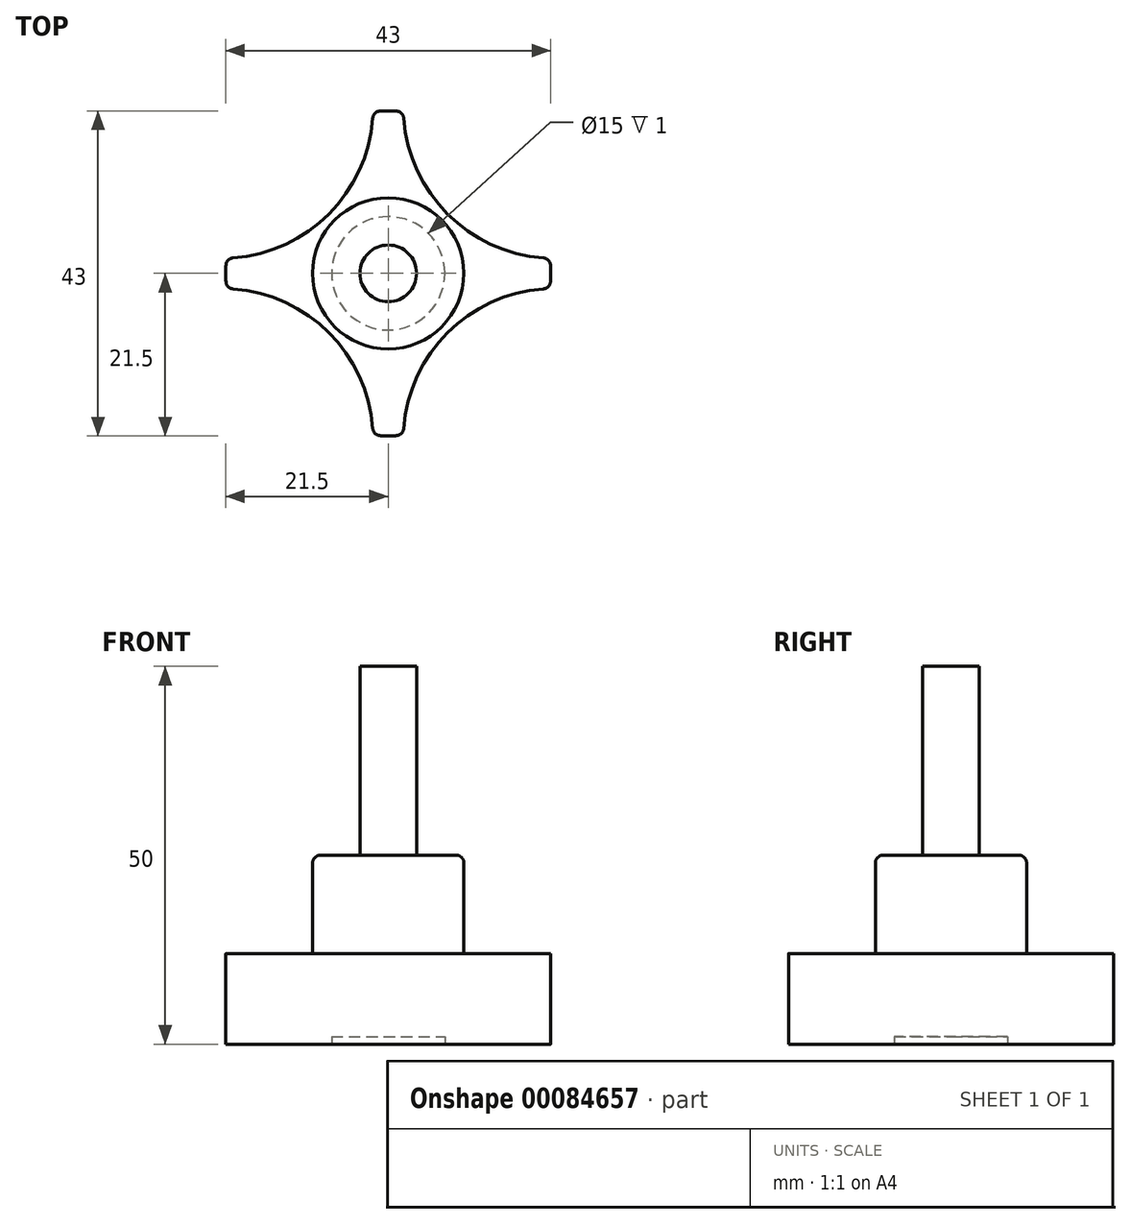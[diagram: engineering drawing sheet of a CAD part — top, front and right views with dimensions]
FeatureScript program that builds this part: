
annotation { "Feature Type Name" : "Feature", "Feature Type Description" : "" }
export const myFeature = defineFeature(function(context is Context, id is Id, definition is map)
    precondition{}
    {
        {
            var Q0;
            Q0=qCreatedBy(makeId("Top.planeOp"),FACE);
            var sketch = newSketch(context, id + "F0", { "sketchPlane" : qUnion([Q0])});
            skLineSegment(sketch, "E0", {"start": v(0, 50) * mm, "end": v(2, 50) * mm});
            skLineSegment(sketch, "E1", {"start": v(50, 0) * mm, "end": v(50, -2) * mm});
            skLineSegment(sketch, "E2.MirrorCS", {"start": v(50, 0) * mm, "end": v(50, 2) * mm});
            skLineSegment(sketch, "E3.MirrorCS", {"start": v(0, -50) * mm, "end": v(2, -50) * mm});
            skLineSegment(sketch, "E4.MirrorCS", {"start": v(-50, 0) * mm, "end": v(-50, 2) * mm});
            skLineSegment(sketch, "E5.MirrorCS", {"start": v(-50, 0) * mm, "end": v(-50, -2) * mm});
            skLineSegment(sketch, "E6.MirrorCS", {"start": v(0, 50) * mm, "end": v(-2, 50) * mm});
            skLineSegment(sketch, "E7.MirrorCS", {"start": v(0, -50) * mm, "end": v(-2, -50) * mm});
            skCircle(sketch, "E8", {"center": v(0, 0) * mm, "radius": 3.75 * mm});
            skCircle(sketch, "E9", {"center": v(0, 0) * mm, "radius": 10 * mm});
            skArc(sketch, "E10", {"start": v(-21.4, 2) * mm, "mid": v(-21.5, 0) * mm, "end": v(-21.4, -2) * mm});
            skLineSegment(sketch, "E11", {"start": v(0, 0) * mm, "end": v(47.67, 47.67) * mm, "construction": true});
            skPoint(sketch, "E12", {"position": v(-21.4, 2) * mm});
            skPoint(sketch, "E13", {"position": v(-2, 21.4) * mm});
            skPoint(sketch, "E14.MirrorP", {"position": v(-21.4, -2) * mm});
            skPoint(sketch, "E15.MirrorP", {"position": v(-2, -21.4) * mm});
            skPoint(sketch, "E16.MirrorP", {"position": v(2, 21.4) * mm});
            skPoint(sketch, "E17.MirrorP", {"position": v(21.4, 2) * mm});
            skPoint(sketch, "E18.MirrorP", {"position": v(21.4, -2) * mm});
            skPoint(sketch, "E19.MirrorP", {"position": v(2, -21.4) * mm});
            skArc(sketch, "E20", {"start": v(21.4, 2) * mm, "mid": v(7.85, 7.85) * mm, "end": v(2, 21.4) * mm});
            skArc(sketch, "E21.MirrorCS", {"start": v(-21.4, 2) * mm, "mid": v(-7.85, 7.85) * mm, "end": v(-2, 21.4) * mm});
            skArc(sketch, "E22.MirrorCS", {"start": v(-21.4, -2) * mm, "mid": v(-7.85, -7.85) * mm, "end": v(-2, -21.4) * mm});
            skArc(sketch, "E23.MirrorCS", {"start": v(21.4, -2) * mm, "mid": v(7.85, -7.85) * mm, "end": v(2, -21.4) * mm});
            skArc(sketch, "E24.trimOffspring", {"start": v(2, 21.4) * mm, "mid": v(0, 21.5) * mm, "end": v(-2, 21.4) * mm});
            skArc(sketch, "E25.trimOffspring", {"start": v(21.4, -2) * mm, "mid": v(21.5, 0) * mm, "end": v(21.4, 2) * mm});
            skArc(sketch, "E26.trimOffspring", {"start": v(-2, -21.4) * mm, "mid": v(0, -21.5) * mm, "end": v(2, -21.4) * mm});
            skSolve(sketch);
        }
        {
            var Q0;
            Q0 = qSketchRegion(id + "F0", true);
            extrude(context, id + "F1", {"entities" : qUnion([Q0]), "depth" : 12 * mm});
        }
        {
            var Q0;
            Q0=makeQuery(id+"F1.opExtrude","SWEPT_EDGE",EDGE,{"disambiguationData":[OSD([sQuery(id+"F0.wireOp",EDGE,"E21.MirrorCS"),sQuery(id+"F0.wireOp",EDGE,"E24.trimOffspring")])]});
            var Q1;
            Q1=makeQuery(id+"F1.opExtrude","SWEPT_EDGE",EDGE,{"disambiguationData":[OSD([sQuery(id+"F0.wireOp",EDGE,"E20"),sQuery(id+"F0.wireOp",EDGE,"E24.trimOffspring")])]});
            var Q2;
            Q2=makeQuery(id+"F1.opExtrude","SWEPT_EDGE",EDGE,{"disambiguationData":[OSD([sQuery(id+"F0.wireOp",EDGE,"E20"),sQuery(id+"F0.wireOp",EDGE,"E25.trimOffspring")])]});
            var Q3;
            Q3=makeQuery(id+"F1.opExtrude","SWEPT_EDGE",EDGE,{"disambiguationData":[OSD([sQuery(id+"F0.wireOp",EDGE,"E23.MirrorCS"),sQuery(id+"F0.wireOp",EDGE,"E25.trimOffspring")])]});
            var Q4;
            Q4=makeQuery(id+"F1.opExtrude","SWEPT_EDGE",EDGE,{"disambiguationData":[OSD([sQuery(id+"F0.wireOp",EDGE,"E23.MirrorCS"),sQuery(id+"F0.wireOp",EDGE,"E26.trimOffspring")])]});
            var Q5;
            Q5=makeQuery(id+"F1.opExtrude","SWEPT_EDGE",EDGE,{"disambiguationData":[OSD([sQuery(id+"F0.wireOp",EDGE,"E22.MirrorCS"),sQuery(id+"F0.wireOp",EDGE,"E26.trimOffspring")])]});
            var Q6;
            Q6=makeQuery(id+"F1.opExtrude","SWEPT_EDGE",EDGE,{"disambiguationData":[OSD([sQuery(id+"F0.wireOp",EDGE,"E10"),sQuery(id+"F0.wireOp",EDGE,"E22.MirrorCS")])]});
            var Q7;
            Q7=makeQuery(id+"F1.opExtrude","SWEPT_EDGE",EDGE,{"disambiguationData":[OSD([sQuery(id+"F0.wireOp",EDGE,"E10"),sQuery(id+"F0.wireOp",EDGE,"E21.MirrorCS")])]});
            fillet(context, id + "F2", {"entities" : qUnion([Q0, Q1, Q2, Q3, Q4, Q5, Q6, Q7]), "radius" : 1 * mm, "tangentPropagation" : true, "allowEdgeOverflow" : false});
        }
        {
            var Q0;
            Q0=makeQuery(id+"F0.imprint","IMPRINT",FACE,{"disambiguationData":[TD([[makeQuery(id+"F0.imprint","IMPRINT",EDGE,{"derivedFrom":sQuery(id+"F0.wireOp",EDGE,"E8")}),-1.0]])]});
            extrude(context, id + "F3", {"entities" : qUnion([Q0]), "operationType" : NewBodyOperationType.ADD, "depth" : 25 * mm});
        }
        {
            var Q0;
            Q0=makeQuery(id+"F0.imprint","IMPRINT",FACE,{"disambiguationData":[TD([[makeQuery(id+"F0.imprint","IMPRINT",EDGE,{"derivedFrom":sQuery(id+"F0.wireOp",EDGE,"E8")}),1.0]])]});
            extrude(context, id + "F4", {"entities" : qUnion([Q0]), "operationType" : NewBodyOperationType.ADD, "depth" : 50 * mm});
        }
        {
            var Q0;
            Q0=makeQuery(id+"F3.opExtrude","CAP_EDGE",EDGE,{"disambiguationData":[OSD([sQuery(id+"F0.wireOp",EDGE,"E9")])],"isStart":false});
            fillet(context, id + "F5", {"entities" : qUnion([Q0]), "radius" : 1 * mm, "tangentPropagation" : true, "allowEdgeOverflow" : false});
        }
        {
            var Q0;
            {var subQ0=sQuery(id+"F0.wireOp",EDGE,"E8");var subQ1=sQuery(id+"F0.wireOp",EDGE,"E9");Q0=makeQuery(id+"F4.boolean.opBoolean","MERGE",FACE,{"derivedFrom":[makeQuery(id+"F3.boolean.opBoolean","MERGE",FACE,{"derivedFrom":[makeQuery(id+"F1.opExtrude","CAP_FACE",FACE,{"disambiguationData":[OSD([subQ1,sQuery(id+"F0.wireOp",EDGE,"E10"),sQuery(id+"F0.wireOp",EDGE,"E20"),sQuery(id+"F0.wireOp",EDGE,"E21.MirrorCS"),sQuery(id+"F0.wireOp",EDGE,"E22.MirrorCS"),sQuery(id+"F0.wireOp",EDGE,"E23.MirrorCS"),sQuery(id+"F0.wireOp",EDGE,"E24.trimOffspring"),sQuery(id+"F0.wireOp",EDGE,"E25.trimOffspring"),sQuery(id+"F0.wireOp",EDGE,"E26.trimOffspring")])],"isStart":true}),makeQuery(id+"F3.opExtrude","CAP_FACE",FACE,{"disambiguationData":[OSD([subQ0,subQ1])],"isStart":true})]}),makeQuery(id+"F4.opExtrude","CAP_FACE",FACE,{"disambiguationData":[OSD([subQ0])],"isStart":true})]});}
            var sketch = newSketch(context, id + "F6", { "sketchPlane" : qUnion([Q0])});
            skCircle(sketch, "E27", {"center": v(0, 0) * mm, "radius": 7.5 * mm});
            skSolve(sketch);
        }
        {
            var Q0;
            Q0 = qSketchRegion(id + "F6", true);
            extrude(context, id + "F7", {"entities" : qUnion([Q0]), "operationType" : NewBodyOperationType.REMOVE, "oppositeDirection" : true, "depth" : 1 * mm});
        }
    });
